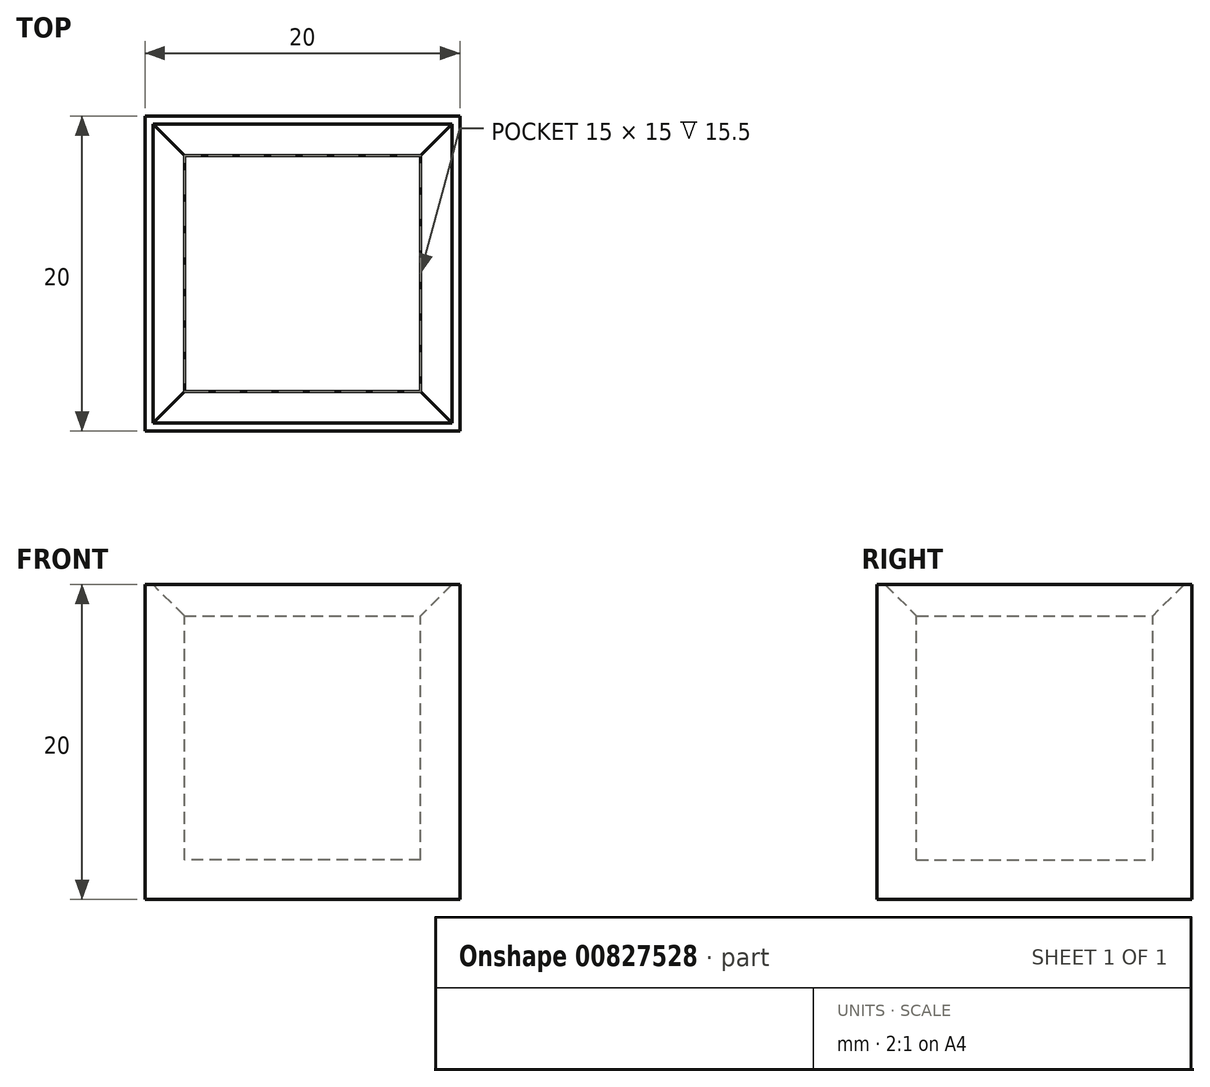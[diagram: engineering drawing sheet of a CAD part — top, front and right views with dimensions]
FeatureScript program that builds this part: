
annotation { "Feature Type Name" : "Feature", "Feature Type Description" : "" }
export const myFeature = defineFeature(function(context is Context, id is Id, definition is map)
    precondition{}
    {
        {
            var Q0;
            Q0=qCreatedBy(makeId("Front.planeOp"),FACE);
            var sketch = newSketch(context, id + "F0", { "sketchPlane" : qUnion([Q0])});
            skLineSegment(sketch, "E0.bottom", {"start": v(0, 0) * mm, "end": v(-20, 0) * mm});
            skLineSegment(sketch, "E0.top", {"start": v(0, 20) * mm, "end": v(-20, 20) * mm});
            skLineSegment(sketch, "E0.left", {"start": v(0, 0) * mm, "end": v(0, 20) * mm});
            skLineSegment(sketch, "E0.right", {"start": v(-20, 0) * mm, "end": v(-20, 20) * mm});
            skSolve(sketch);
        }
        {
            var Q0;
            Q0 = qSketchRegion(id + "F0", true);
            extrude(context, id + "F1", {"entities" : qUnion([Q0]), "depth" : 20 * mm, "offsetDistance" : 25 * mm});
        }
        {
            var Q0;
            Q0=makeQuery(id+"F1.opExtrude","SWEPT_FACE",FACE,{"disambiguationData":[OSD([sQuery(id+"F0.wireOp",EDGE,"E0.top")])]});
            shell(context, id + "F2", {"entities" : qUnion([Q0]), "thickness" : 2.5 * mm});
        }
        {
            var Q0;
            Q0=makeQuery(id+"F2.opShell","OFFSET_EDGE",EDGE,{"disambiguationData":[OSD([sQuery(id+"F0.wireOp",EDGE,"E0.top"),sQuery(id+"F0.wireOp",EDGE,"E0.right")])]});
            var Q1;
            {var subQ0=sQuery(id+"F0.wireOp",EDGE,"E0.top");Q1=makeQuery(id+"F2.opShell","OFFSET_EDGE",EDGE,{"disambiguationData":[OSD([subQ0]),TDD([makeQuery(id+"F1.opExtrude","CAP_EDGE",EDGE,{"disambiguationData":[OSD([subQ0])],"isStart":true})])]});}
            var Q2;
            Q2=makeQuery(id+"F2.opShell","OFFSET_EDGE",EDGE,{"disambiguationData":[OSD([sQuery(id+"F0.wireOp",EDGE,"E0.top"),sQuery(id+"F0.wireOp",EDGE,"E0.left")])]});
            var Q3;
            {var subQ0=sQuery(id+"F0.wireOp",EDGE,"E0.top");Q3=makeQuery(id+"F2.opShell","OFFSET_EDGE",EDGE,{"disambiguationData":[OSD([subQ0]),TDD([makeQuery(id+"F1.opExtrude","CAP_EDGE",EDGE,{"disambiguationData":[OSD([subQ0])],"isStart":false})])]});}
            chamfer(context, id + "F3", {"entities" : qUnion([Q0, Q1, Q2, Q3]), "width" : 2 * mm, "tangentPropagation" : true});
        }
    });
